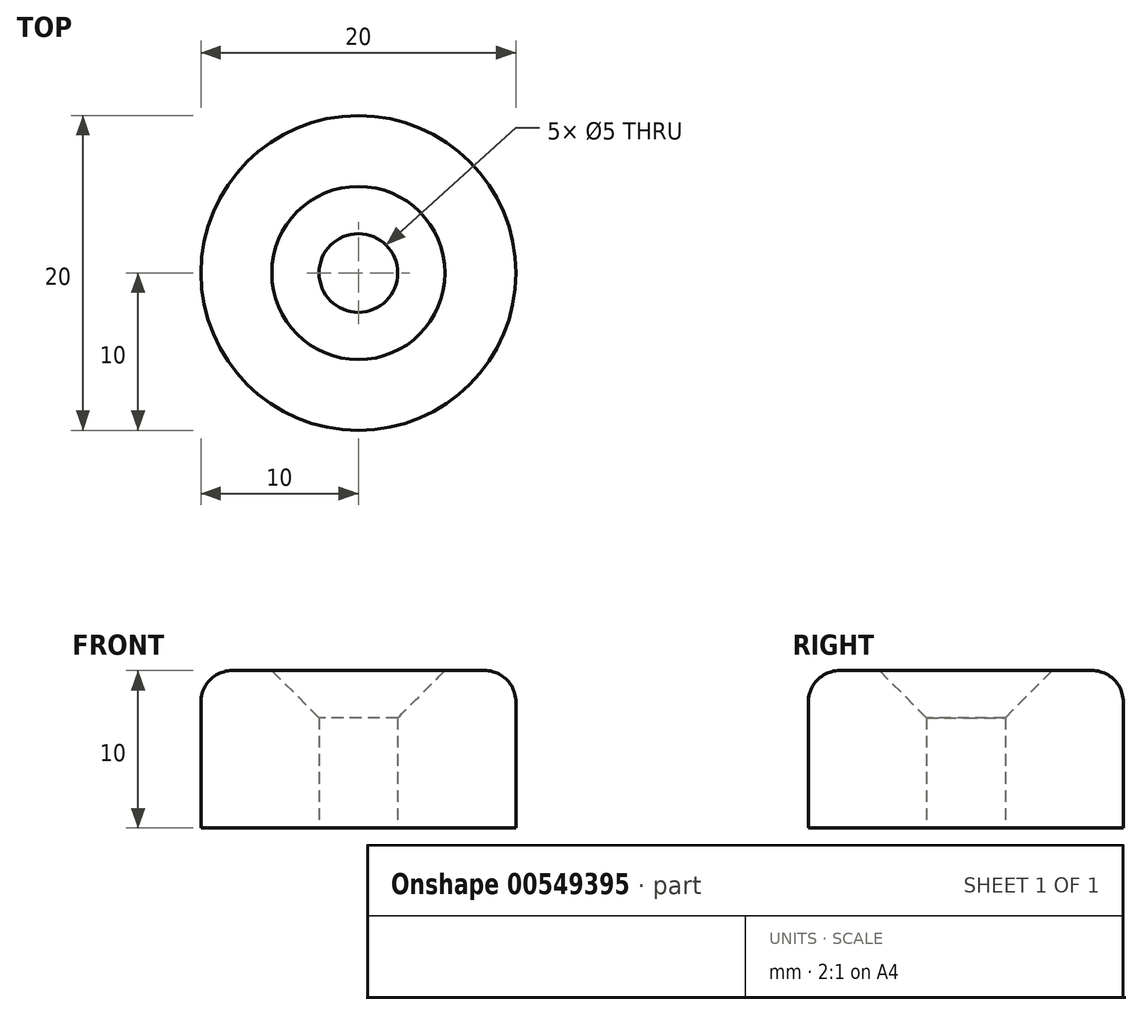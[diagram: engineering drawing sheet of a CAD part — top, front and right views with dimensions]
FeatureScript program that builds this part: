
annotation { "Feature Type Name" : "Feature", "Feature Type Description" : "" }
export const myFeature = defineFeature(function(context is Context, id is Id, definition is map)
    precondition{}
    {
        {
            var Q0;
            Q0=qCreatedBy(makeId("Top.planeOp"),FACE);
            var sketch = newSketch(context, id + "F0", { "sketchPlane" : qUnion([Q0])});
            skCircle(sketch, "E0", {"center": v(0, 0) * mm, "radius": 10 * mm});
            skCircle(sketch, "E1", {"center": v(0, 0) * mm, "radius": 2.5 * mm});
            skSolve(sketch);
        }
        {
            var Q0;
            Q0=makeQuery(id+"F0.imprint","IMPRINT",FACE,{"disambiguationData":[TD([[makeQuery(id+"F0.imprint","IMPRINT",EDGE,{"derivedFrom":sQuery(id+"F0.wireOp",EDGE,"E0")}),1.0]])]});
            extrude(context, id + "F1", {"entities" : qUnion([Q0]), "depth" : 10 * mm, "offsetDistance" : 25 * mm});
        }
        {
            var Q0;
            Q0=makeQuery(id+"F1.opExtrude","CAP_EDGE",EDGE,{"disambiguationData":[OSD([sQuery(id+"F0.wireOp",EDGE,"E1")])],"isStart":false});
            chamfer(context, id + "F2", {"entities" : qUnion([Q0]), "width" : 3 * mm, "tangentPropagation" : true});
        }
        {
            var Q0;
            Q0=makeQuery(id+"F1.opExtrude","CAP_EDGE",EDGE,{"disambiguationData":[OSD([sQuery(id+"F0.wireOp",EDGE,"E0")])],"isStart":false});
            fillet(context, id + "F3", {"entities" : qUnion([Q0]), "radius" : 2 * mm, "tangentPropagation" : true, "allowEdgeOverflow" : false});
        }
    });
